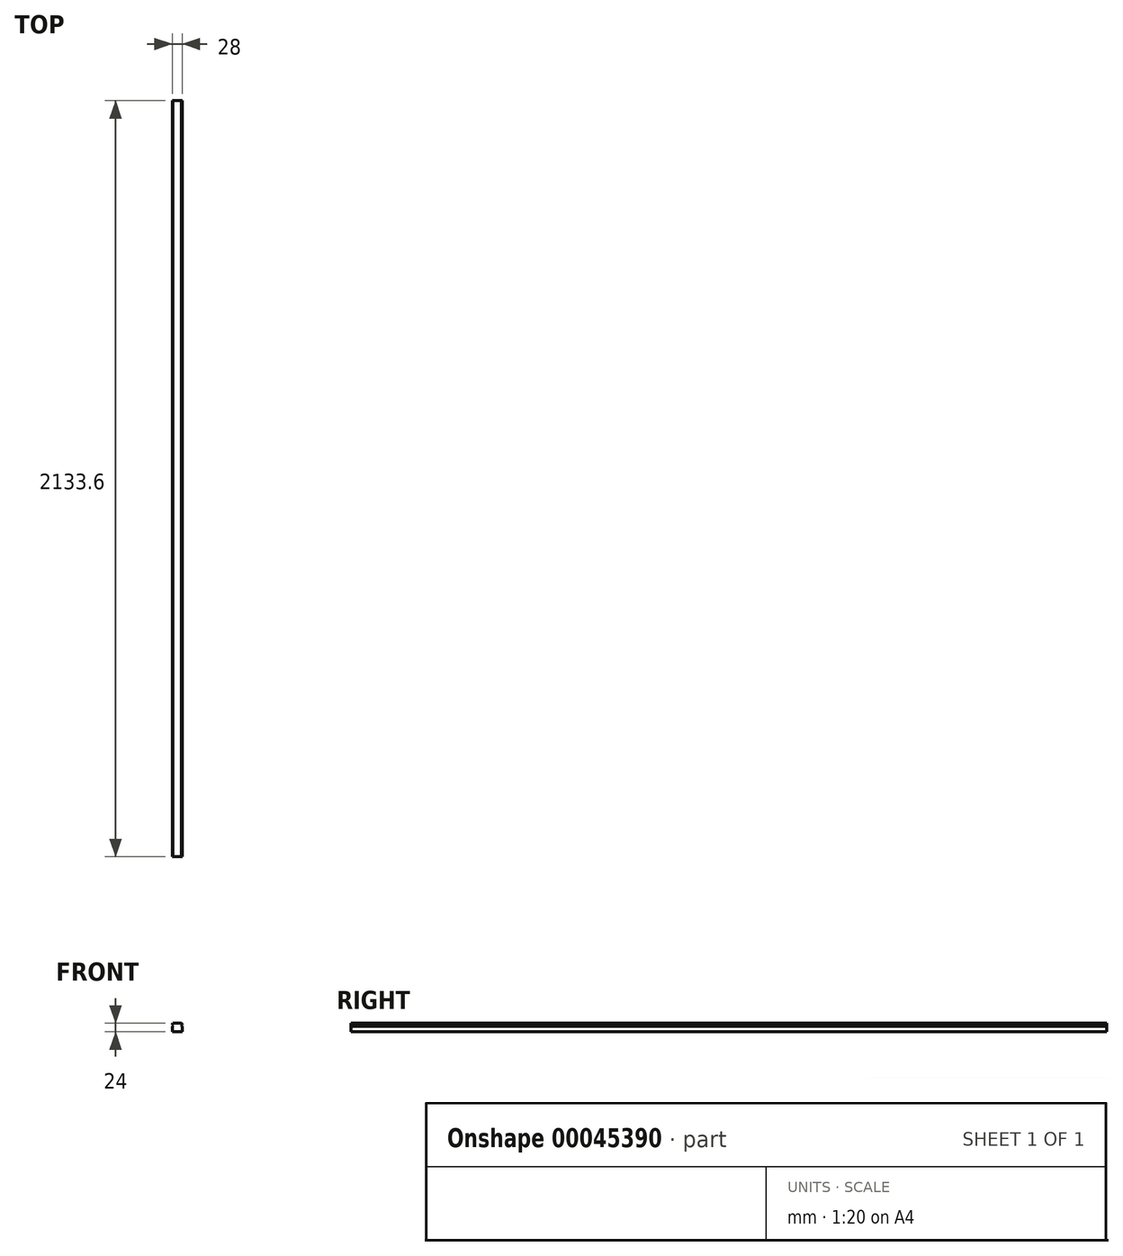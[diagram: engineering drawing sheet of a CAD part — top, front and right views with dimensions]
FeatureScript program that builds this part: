
annotation { "Feature Type Name" : "Feature", "Feature Type Description" : "" }
export const myFeature = defineFeature(function(context is Context, id is Id, definition is map)
    precondition{}
    {
        {
            var Q0;
            Q0=qCreatedBy(makeId("Front.planeOp"),FACE);
            var sketch = newSketch(context, id + "F0", { "sketchPlane" : qUnion([Q0])});
            skLineSegment(sketch, "E0.bottom", {"start": v(-9.9, 12.6) * mm, "end": v(13.87, 12.6) * mm});
            skLineSegment(sketch, "E0.top", {"start": v(-12.01, -11.4) * mm, "end": v(15.99, -11.4) * mm});
            skLineSegment(sketch, "E0.left", {"start": v(-12.01, 10.49) * mm, "end": v(-12.01, 9.49) * mm});
            skLineSegment(sketch, "E0.right", {"start": v(15.99, 10.49) * mm, "end": v(15.99, 9.49) * mm});
            skLineSegment(sketch, "E1", {"start": v(-9.9, 12.6) * mm, "end": v(-12.01, 10.49) * mm});
            skLineSegment(sketch, "E2", {"start": v(13.87, 12.6) * mm, "end": v(15.99, 10.49) * mm});
            skLineSegment(sketch, "E3", {"start": v(-12.01, 9.49) * mm, "end": v(-9.18, 6.66) * mm});
            skLineSegment(sketch, "E4", {"start": v(-9.18, 6.66) * mm, "end": v(-12.01, 3.83) * mm});
            skLineSegment(sketch, "E5", {"start": v(15.99, 9.49) * mm, "end": v(13.16, 6.66) * mm});
            skLineSegment(sketch, "E6", {"start": v(13.16, 6.66) * mm, "end": v(15.99, 3.83) * mm});
            skLineSegment(sketch, "E7.trimOffspring", {"start": v(-12.01, 3.83) * mm, "end": v(-12.01, -11.4) * mm});
            skLineSegment(sketch, "E8.trimOffspring", {"start": v(15.99, 3.83) * mm, "end": v(15.99, -11.4) * mm});
            skSolve(sketch);
        }
        {
            var Q0;
            Q0=qSketchRegion(id+"F0",true);
            extrude(context, id + "F1", {"entities" : qUnion([Q0]), "depth" : 2133.6 * mm});
        }
    });
